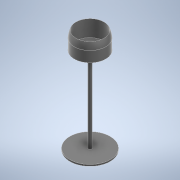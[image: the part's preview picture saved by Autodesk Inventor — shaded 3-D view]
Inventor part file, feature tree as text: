
AUTODESK INVENTOR PART (.ipt)
format: ipt  version: 2021 (Build 250183000, 183)  size: 121,856 bytes
history: native  units: mm
features: revolve x1, fillet x1, sketch x1
ambient origin geometry x8: Origin, YZ Plane, XZ Plane, XY Plane, X Axis, Y Axis, Z Axis, Center Point
bodies: Solid1 (feature_tree)
feature tree (3):
  revolve  "Revolution1"  [1 undecoded]
  fillet  "Fillet1"  [1 undecoded]
  sketch  "Sketch1"  dims[d0=90.0deg d1=2.0mm]
note: 2 required parameter values undecoded (feature->parameter linkage not recoverable at this tier; creation-order binding heuristic only, values carry confidence <= 0.55)